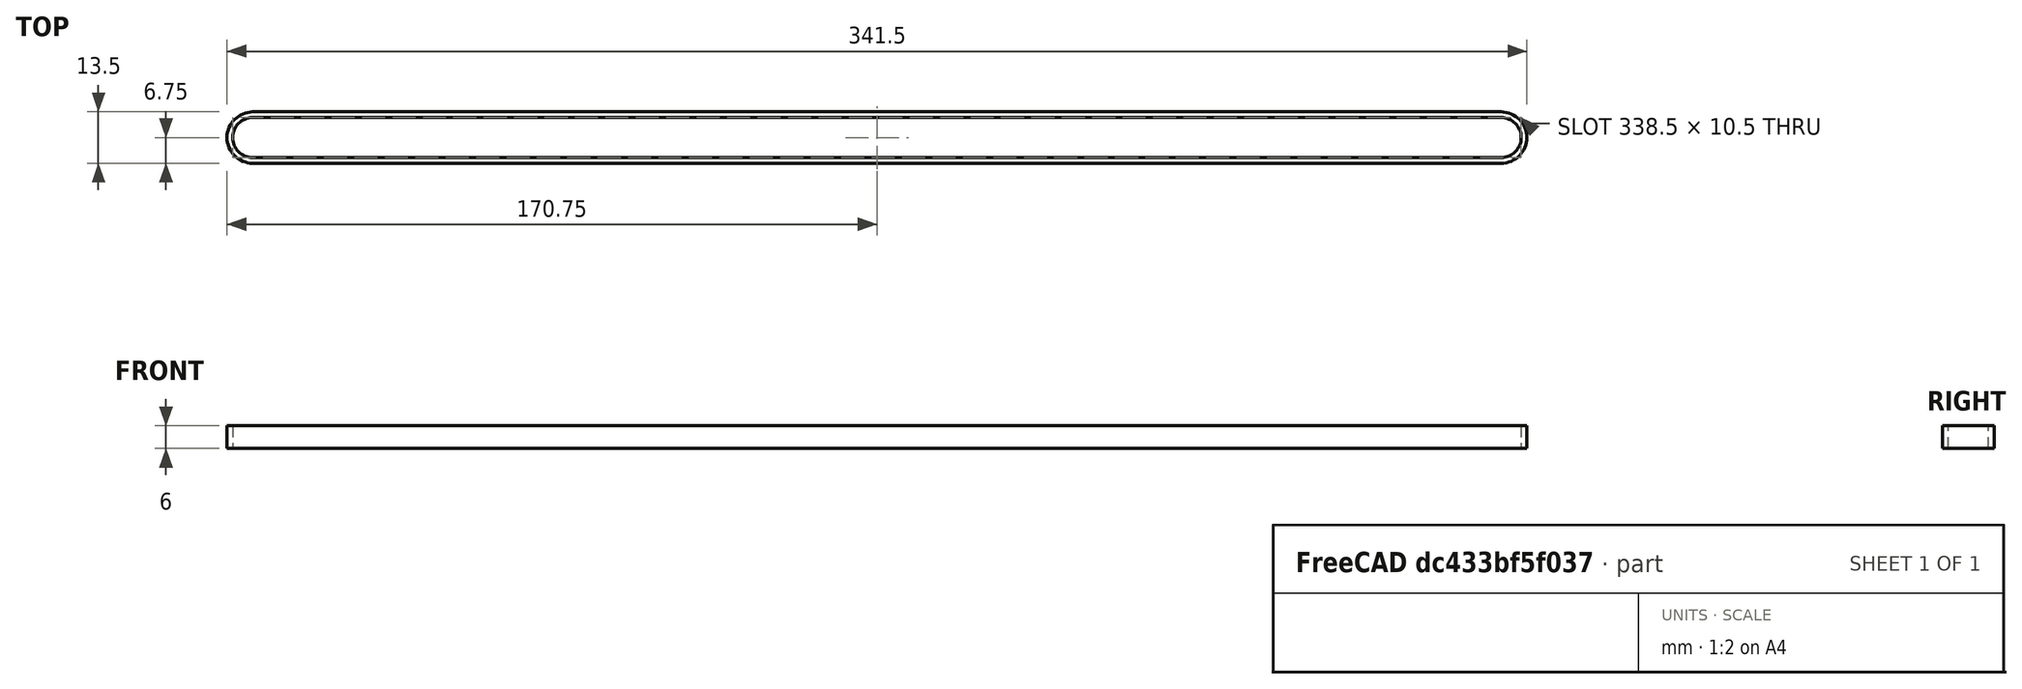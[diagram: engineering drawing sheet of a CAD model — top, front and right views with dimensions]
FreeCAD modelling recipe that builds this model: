
FCSTD DOCUMENT  (FreeCAD 0.14R3310 (Git))
Label: 58. CORREA GT2 (SIN DIENTES)
License: CC-BY 3.0
LicenseURL: http://creativecommons.org/licenses/by/3.0/
objects: Sketcher::SketchObject×1, PartDesign::Pad×1
note: 3 computed .brp shape members not serialized (recipe doc carries the construction recipe); baked Part::Feature solids carry a one-line shape summary decoded from their .brp

FEATURE [Sketcher::SketchObject] Sketch
  sketch-geometry (8):
    g0: LineSegment StartX=-164 StartY=5.25 StartZ=0 EndX=164 EndY=5.25 EndZ=0
    g1: ArcOfCircle CenterX=164 CenterY=0 CenterZ=0 NormalX=0 NormalY=0 NormalZ=1 Radius=5.25 StartAngle=4.71239 EndAngle=7.85398
    g2: LineSegment StartX=164 StartY=-5.25 StartZ=0 EndX=-164 EndY=-5.25 EndZ=0
    g3: ArcOfCircle CenterX=-164 CenterY=0 CenterZ=0 NormalX=0 NormalY=0 NormalZ=1 Radius=5.25 StartAngle=1.5708 EndAngle=4.71238
    g4: ArcOfCircle CenterX=-164 CenterY=0 CenterZ=0 NormalX=0 NormalY=0 NormalZ=1 Radius=6.75 StartAngle=1.5708 EndAngle=4.71239
    g5: LineSegment StartX=-164 StartY=6.75 StartZ=0 EndX=164 EndY=6.75 EndZ=0
    g6: LineSegment StartX=-164 StartY=-6.75 StartZ=0 EndX=164 EndY=-6.75 EndZ=0
    g7: ArcOfCircle CenterX=164 CenterY=0 CenterZ=0 NormalX=0 NormalY=0 NormalZ=1 Radius=6.75 StartAngle=4.71239 EndAngle=7.85398
  constraints (27):
    c: Distance(g0) = 328
    c: Symmetric(g0,g0,g-2)
    c: PointOnObject(g1,g-1)
    c: Coincident(g1,g0)
    c: Tangent(g1,g0)
    c: Radius(g1) = 5.25
    c: Coincident(g2,g1)
    c: Horizontal(g2)
    c: Equal(g2,g0)
    c: Tangent(g2,g1)
    c: PointOnObject(g3,g-1)
    c: Coincident(g3,g0)
    c: Coincident(g3,g2)
    c: Coincident(g4,g3)
    c: Coincident(g5,g4)
    c: Horizontal(g5)
    c: Tangent(g5,g4)
    c: Radius(g4) = 6.75
    c: Equal(g5,g0)
    c: Coincident(g6,g4)
    c: Horizontal(g6)
    c: Equal(g6,g5)
    c: Tangent(g6,g4)
    c: Coincident(g7,g1)
    c: Coincident(g7,g5)
    c: Coincident(g7,g6)
    c: Tangent(g7,g6)
FEATURE [PartDesign::Pad] Pad
  Length = 6
  Length2 = 100
  Sketch = -> Sketch
  Type = 0
